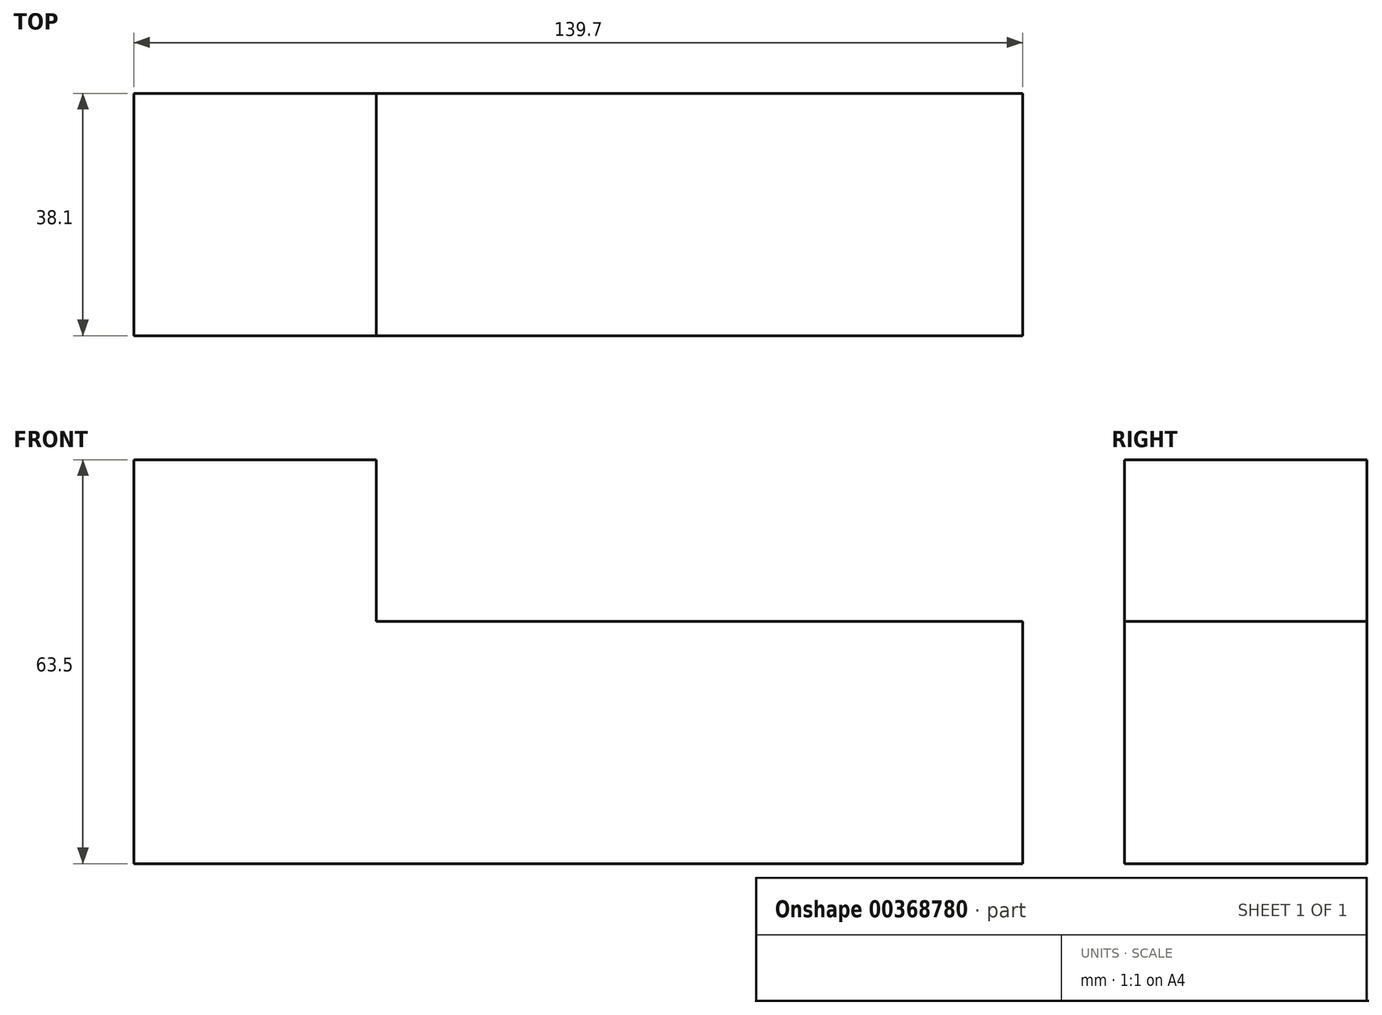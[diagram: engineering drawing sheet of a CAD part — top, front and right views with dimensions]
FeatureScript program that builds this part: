
annotation { "Feature Type Name" : "Feature", "Feature Type Description" : "" }
export const myFeature = defineFeature(function(context is Context, id is Id, definition is map)
    precondition{}
    {
        {
            var Q0;
            Q0=qCreatedBy(makeId("Front.planeOp"),FACE);
            var sketch = newSketch(context, id + "F0", { "sketchPlane" : qUnion([Q0])});
            skLineSegment(sketch, "E0", {"start": v(-79.42, 63.5) * mm, "end": v(-79.42, 0) * mm});
            skLineSegment(sketch, "E1", {"start": v(-79.42, 0) * mm, "end": v(60.28, 0) * mm});
            skLineSegment(sketch, "E2", {"start": v(-79.42, 63.5) * mm, "end": v(-41.32, 63.5) * mm});
            skLineSegment(sketch, "E3", {"start": v(-41.32, 63.5) * mm, "end": v(-41.32, 38.1) * mm});
            skLineSegment(sketch, "E4", {"start": v(-41.32, 38.1) * mm, "end": v(60.28, 38.1) * mm});
            skLineSegment(sketch, "E5", {"start": v(60.28, 38.1) * mm, "end": v(60.28, 0) * mm});
            skSolve(sketch);
        }
        {
            var Q0;
            Q0=makeQuery(id+"F0.imprint","IMPRINT",FACE,{"disambiguationData":[TD([[makeQuery(id+"F0.imprint","IMPRINT",EDGE,{"derivedFrom":sQuery(id+"F0.wireOp",EDGE,"E0")}),1.0]])]});
            extrude(context, id + "F1", {"entities" : qUnion([Q0]), "depth" : 38.1 * mm});
        }
    });
